# Revit family: BoelsRental_ScissorLift_JLG_2646ESa
name_source: partatom
category: Site
units: mm (PartAtom-declared; Revit-internal decimal feet)

## family parameters
Always vertical = Yes
Cut with Voids When Loaded = No
OmniClass Number = 23.50.05.14.11
OmniClass Title = Scissors Lifts
Part Type = Normal
Round Connector Dimension = Use Diameter
Shared = No
Work Plane-Based = No

## types (1)
- 2646ES
    Assembly Code = E1030100
    AssetType = Movable
    BIMObjectName = BoelsRental_ScissorLift_JLG_2646ES
    BoelsSubgroup = 18081 - Scissor lift 9.9m battery
    ClassificationName = Uniclass2015
    ClassificationValue = Pr_65_80_47_95
    Cost = 0 $
    DeepCycleBatteries = 4 x 6v 220 Ah
    Description = SCISSOR LIFT, SELF-PROPELLED, PLATFORM WIDTH > 90 CM, ELEC. < 9 M
    DocumentationCertificates = https://www.boels.com
    DocumentationInstallationGuide = https://www.boels.com
    DocumentationLiterature = https://www.boels.com
    DocumentationMaintenance = https://www.boels.com
    DocumentationTechnical = https://www.boels.com
    Drive = 24v Electric 6 kW
    DriveSpeedElevator = 1 kph (0.61 mph)
    DriveSpeedLowered = 4 kph (2.48 mph)
    DurationUnit = Years
    ExpectedLife = 0
    Gradeability = 25%
    GrossVehicleWeightANSI = 2302 kg (5075 lbs)
    GrossVehicleWeightCE = 2783 kg (6135 lbs)
    GroundClearance = 0.13 m (0 ft  5 in)
    HydraulicSystem = 20 L (4.40 gal)
    IfcExportAs = IfcTransportElement
    IfcExportType = IfcTransportElementType
    Keynote = X
    LiftUpTime = 40 sec
    LowerDownTime = 50 sec
    Manufacturer = Boels Rental (JLG)
    ManufacturerName = Boels Rental (JLG)
    Material = Steel
    MaxGroundBearingPressureANSI = 6.98kg/cm2 (99.27 psi)
    MaxGroundBearingPressureCE = 6.98 kg/cm2 (99.27 psi)
    Model = Scissor Lift - 2646ES
    ModelNumber = 2646ES
    ModelReference = Scissor Lift
    NBSDescription = Vertical lifting platforms
    NBSObjectName = Boels Rental - Vertical lifting platforms
    NBSReference = 90-80-65/350
    NominalDepth = 0 mm  [stored 0 ft]
    NominalHeight = 0 mm  [stored 0 ft]
    NominalLength = 0 mm  [stored 0 ft]
    PS = 2500 mm  [stored 8.2021 ft]
    PlatformCapacityANSI = 454kg (1000 lbs)
    PlatformCapacityCE = 450kg (992 lbs)
    PlatformExtentionCapacityANSI = 113kg (250 lbs)
    PlatformExtentionCapacityCE = 120kg (264 lbs)
    PlatformExtentionSize = 1.22 m (4 ft  0 in)
    PlatformSize = 1.12 m x 2.50 m (3 ft  8 in x 8 ft  2.5 in)
    ProductPageLink = https://www.boels.com
    ProductionYear = 2022
    RaisedPlatformHeight = 7.96 m (26 ft  1 in)
    Static = 763 mm
    TurningRadiusInside = 0
    TurningRadiusOutside = 2.41 m (7 ft 11 in)
    Type Comments = Scissor Lift - 2646ES
    TypeName = Scissor Lift - 2646ES
    URL = https://www.boels.com
    WarrantyDurationLabor = 0
    WarrantyDurationParts = 0
    WarrantyDurationUnit = Years
    WarrantyGuarantorLabor = https://www.boels.com
    WarrantyGuarantorParts = https://www.boels.com
    _BSBibleVersion = 16
    _BimSpecGuid = 0
    _CurrentRevision = 1
    _DistributedBy = https://www.boels.com
    _ObjectUserGuide = https://www.boels.com

note: [stored X ft] marks values corroborated as IEEE doubles in the binary element streams (Revit-internal decimal feet)

## geometry (parser evidence)
native form markers: Sweep x54
no freeform markers — native parametric forms only
